# Revit family: LBRP-M-LSSL-4SQD
name_source: partatom
category: Lighting Fixtures
units: mm (PartAtom-declared; Revit-internal decimal feet)

## family parameters
Cut with Voids When Loaded = No
Host = Face
Light Source = Yes
OmniClass Number = 23.80.70.11.14.17
OmniClass Title = Direct/Indirect
Part Type = Normal
Room Calculation Point = No
Round Connector Dimension = Use Diameter
Shared = Yes

## types (1)
- LBRP-M-LSSL-4SQD
    A = 4.24 "
    Apparent Load = 12 VA
    Assembly Code = D5020200
    B = 5.86 "
    C = 0.2 "
    Color Filter = 16777215
    D = 5.97 "
    Default Elevation = 48 "
    Description = PRO CANLESS DIRECT INSTALL DOWNLIGHT
    Dimming Lamp Color Temperature Shift = <None>
    Features = 4", 6" and 8" apertures, delivering 800 to 5000 lumens
•  Aluminum anodized or white reflector with cast flange, 55 deg cutoff
•  Switchable Lumen, CCT, and Beam Angle
•  Integral wiring compartment (standard)
•  Optional support pans for Joist or T-Grid ceilings
•  Universal 120–277V with 0–10V Dim to Off
•  Long Life L70 at >50,000 hrs (TM-21),
    Glass = White Glass
    Heat Sink = Black
    Housing Material = Paint - Matte White
    Lamp = LED's
    Load Classification = Lighting
    Manufacturer = Prescolite Lighting
    Model = LBRP-M-LSSL-4SQD
    Photometric Notes = More IES files download on Photometric Web Link
    Photometric Web File = LBRP-M-LSMLCS9_LBRP-4SQD-T-D_3000K_1600lm.ies
    Power Factor = 0.9
    Tilt Angle = -90.00°
    URL = https://www.currentlighting.com
    Voltage = 120 V
    Warranty = 5-Years Warranty
    Wattage Comments = 9.6 - 29.7 W
    zz Length 1 = 48 "

## geometry (parser evidence)
native form markers: Sweep x2
no freeform markers — native parametric forms only
